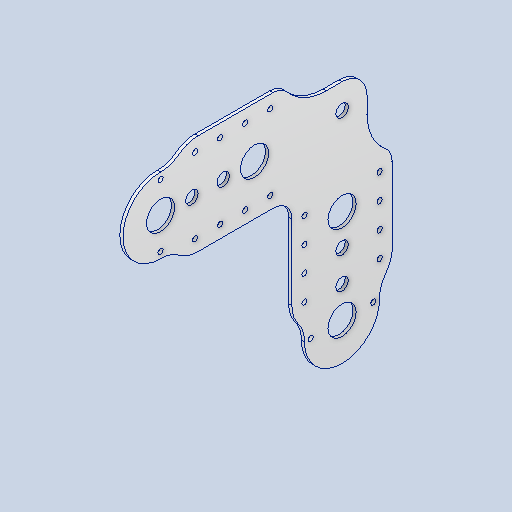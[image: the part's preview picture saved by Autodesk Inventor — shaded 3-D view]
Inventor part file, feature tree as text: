
AUTODESK INVENTOR PART (.ipt)
format: ipt  version: 2025.1 (Build 291241020, 241B)  size: 250,368 bytes
history: native  units: in
note: dims shown in document units (in); Inventor stores cm internally (conversion verified against a paired STEP export)
features: fillet x3, sketch x2, extrude x1
ambient origin geometry x8: Origin, YZ Plane, XZ Plane, XY Plane, X Axis, Y Axis, Z Axis, Center Point
bodies: Solid1 (feature_tree)
feature tree (6):
  extrude  "Extrusion1"  Depth=4.0in
  fillet  "Fillet1"  Radius=1.125in
  fillet  "Fillet2"  Radius=0.5in
  fillet  "Fillet3"  Radius=0.5in
  sketch  "Sketch Rectangular Pattern1"  dims[d0=4.0in d1=6.0in d2=1.125in d3=0.5in d4=0.5in]
  sketch  "Sketch Circular Pattern1"  dims[d5=1.125in d6=1.25in d7=1.25in d8=1.25in d9=0.2087in d10=0.5in d11=0.5in d12=2.3622in d14=1.0in d15=0.7874in d17=3.0in d20=0.125in d21=0.0in d22=0.5in d24=7.2441in d25=1.0in d26=2.0in d27=135.0deg d28=2.0in d29=1.0in d30=0.75in d31=2.0in d32=3.0in d33=1.25in d34=1.25in d35=0.75in d36=0.75in d37=0.7874in d39=90.0deg d41=1.25in d23=0.0344in]
